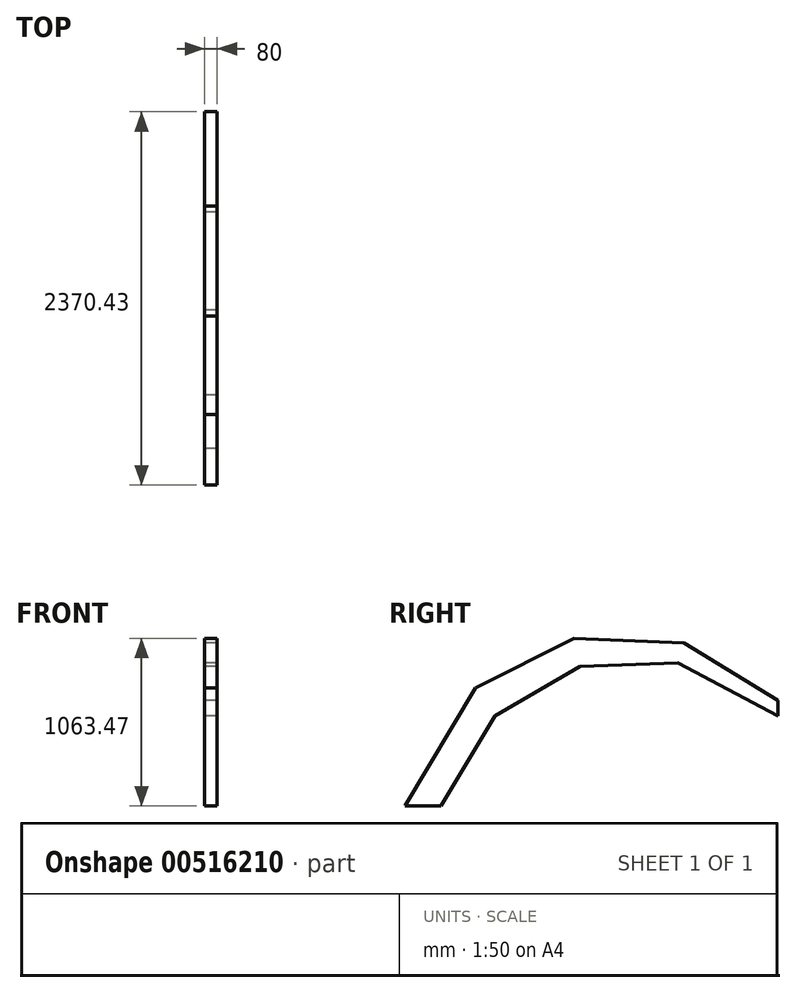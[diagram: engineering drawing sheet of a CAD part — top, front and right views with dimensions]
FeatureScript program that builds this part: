
annotation { "Feature Type Name" : "Feature", "Feature Type Description" : "" }
export const myFeature = defineFeature(function(context is Context, id is Id, definition is map)
    precondition{}
    {
        {
            var Q0;
            Q0=qCreatedBy(makeId("Right.planeOp"),FACE);
            var sketch = newSketch(context, id + "F0", { "sketchPlane" : qUnion([Q0])});
            skLineSegment(sketch, "E0", {"start": v(0, 0) * mm, "end": v(447.11, 750.5) * mm});
            skLineSegment(sketch, "E1", {"start": v(447.11, 750.5) * mm, "end": v(1073.25, 1063.47) * mm});
            skLineSegment(sketch, "E2", {"start": v(1772.63, 1034.2) * mm, "end": v(2370.43, 670) * mm});
            skLineSegment(sketch, "E3", {"start": v(2370.43, 670) * mm, "end": v(2370.43, 570) * mm});
            skLineSegment(sketch, "E4", {"start": v(570.43, 570) * mm, "end": v(230, 0) * mm});
            skLineSegment(sketch, "E5", {"start": v(230, 0) * mm, "end": v(0, 0) * mm});
            skLineSegment(sketch, "E6", {"start": v(1073.25, 1063.47) * mm, "end": v(1772.63, 1034.2) * mm});
            skLineSegment(sketch, "E7", {"start": v(115, 0) * mm, "end": v(450, 580.24) * mm, "construction": true});
            skLineSegment(sketch, "E8", {"start": v(570.43, 570) * mm, "end": v(1111.47, 884.88) * mm});
            skLineSegment(sketch, "E9", {"start": v(1111.47, 884.88) * mm, "end": v(1734.5, 908.5) * mm});
            skLineSegment(sketch, "E10", {"start": v(1734.5, 908.5) * mm, "end": v(2370.43, 570) * mm});
            skArc(sketch, "E11", {"start": v(2370.43, 670) * mm, "mid": v(985.47, 1041.7) * mm, "end": v(0, 0) * mm, "construction": true});
            skArc(sketch, "E12", {"start": v(2370.43, 570) * mm, "mid": v(1138.47, 892.38) * mm, "end": v(230, 0) * mm, "construction": true});
            skLineSegment(sketch, "E13", {"start": v(1073.25, 1063.47) * mm, "end": v(1129.12, 802.41) * mm, "construction": true});
            skLineSegment(sketch, "E14", {"start": v(1772.63, 1034.2) * mm, "end": v(1697.92, 787.9) * mm, "construction": true});
            skSolve(sketch);
        }
        {
            var Q0;
            Q0=qSketchRegion(id+"F0",true);
            extrude(context, id + "F1", {"entities" : qUnion([Q0]), "depth" : 80 * mm, "offsetDistance" : 25 * mm});
        }
    });
